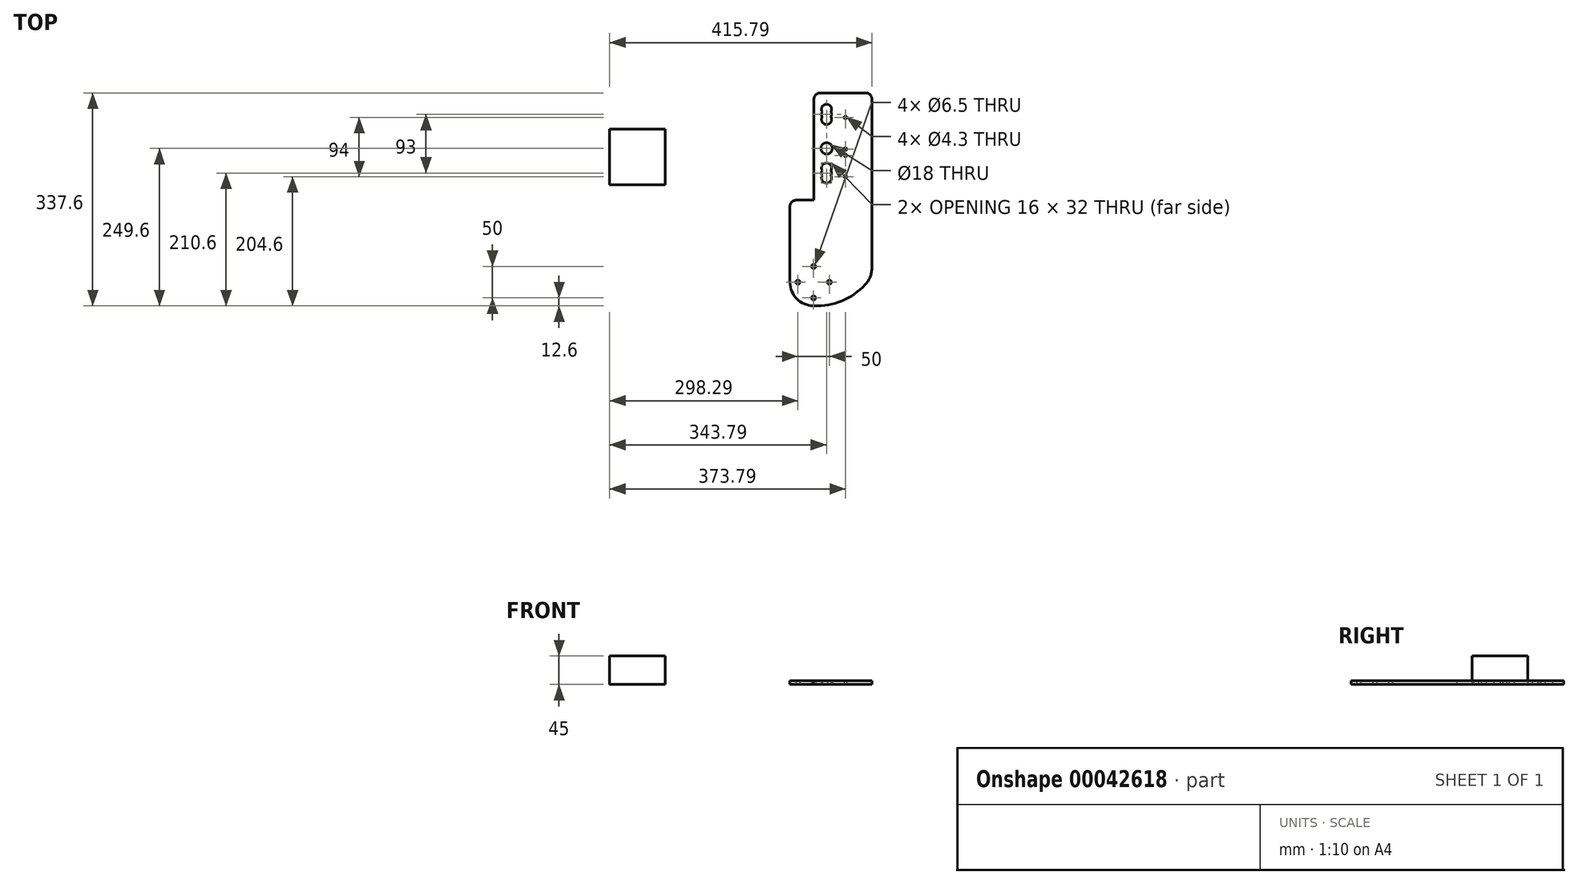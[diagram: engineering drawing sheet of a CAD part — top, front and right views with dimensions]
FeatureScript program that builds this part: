
annotation { "Feature Type Name" : "Feature", "Feature Type Description" : "" }
export const myFeature = defineFeature(function(context is Context, id is Id, definition is map)
    precondition{}
    {
        {
            var Q0;
            Q0=qCreatedBy(makeId("Top.planeOp"),FACE);
            var sketch = newSketch(context, id + "F0", { "sketchPlane" : qUnion([Q0])});
            skCircle(sketch, "E0", {"center": v(0, 0) * mm, "radius": 25 * mm, "construction": true});
            skLineSegment(sketch, "E1", {"start": v(-37.5, 0) * mm, "end": v(-37.5, 250) * mm});
            skLineSegment(sketch, "E2", {"start": v(-37.5, 0) * mm, "end": v(162.5, 0) * mm, "construction": true});
            skLineSegment(sketch, "E3.top", {"start": v(-27.5, 130) * mm, "end": v(50.5, 130) * mm});
            skLineSegment(sketch, "E3.left", {"start": v(-37.5, 29.98) * mm, "end": v(-37.5, 130) * mm});
            skLineSegment(sketch, "E3.right", {"start": v(50.5, 42) * mm, "end": v(50.5, 130) * mm, "construction": true});
            skLineSegment(sketch, "E4.bottom", {"start": v(-115.86, -29.09) * mm, "end": v(-157.06, -29.09) * mm});
            skLineSegment(sketch, "E4.top", {"start": v(-115.86, 126.35) * mm, "end": v(-157.06, 126.35) * mm});
            skLineSegment(sketch, "E4.left", {"start": v(-115.86, -29.09) * mm, "end": v(-115.86, 126.35) * mm});
            skLineSegment(sketch, "E4.right", {"start": v(-157.06, -29.09) * mm, "end": v(-157.06, 126.35) * mm});
            skPoint(sketch, "E5", {"position": v(-152.04, 2.91) * mm});
            skPoint(sketch, "E6", {"position": v(-152.03, 36.91) * mm});
            skPoint(sketch, "E7", {"position": v(-152.04, 46.91) * mm});
            skPoint(sketch, "E8", {"position": v(-152.05, 96.91) * mm});
            skLineSegment(sketch, "E9", {"start": v(50.5, 130) * mm, "end": v(50.5, 167) * mm, "construction": true});
            skLineSegment(sketch, "E10", {"start": v(50.5, 167) * mm, "end": v(50.5, 305.99) * mm, "construction": true});
            skPoint(sketch, "E11", {"position": v(50.5, 167) * mm});
            skPoint(sketch, "E12", {"position": v(50.5, 201) * mm});
            skPoint(sketch, "E13", {"position": v(50.5, 211) * mm});
            skPoint(sketch, "E14", {"position": v(50.5, 261) * mm});
            skLineSegment(sketch, "E15.bottom", {"start": v(50.5, 130) * mm, "end": v(92.5, 130) * mm, "construction": true});
            skLineSegment(sketch, "E15.top", {"start": v(50.5, 276) * mm, "end": v(92.5, 276) * mm, "construction": true});
            skLineSegment(sketch, "E15.left", {"start": v(50.5, 130) * mm, "end": v(50.5, 276) * mm, "construction": true});
            skLineSegment(sketch, "E15.right", {"start": v(92.5, 130) * mm, "end": v(92.5, 276) * mm, "construction": true});
            skLineSegment(sketch, "E16.0", {"start": v(20.5, 160) * mm, "end": v(20.5, 305.99) * mm, "construction": true});
            skPoint(sketch, "E17", {"position": v(20.5, 212) * mm});
            skPoint(sketch, "E18", {"position": v(20.5, 181) * mm});
            skPoint(sketch, "E19", {"position": v(20.5, 173) * mm});
            skPoint(sketch, "E20", {"position": v(20.5, 165) * mm});
            skPoint(sketch, "E21", {"position": v(20.5, 274) * mm});
            skPoint(sketch, "E22", {"position": v(20.5, 266) * mm});
            skPoint(sketch, "E23", {"position": v(20.5, 258) * mm});
            skCircle(sketch, "E24", {"center": v(50.5, 167) * mm, "radius": 2.15 * mm});
            skCircle(sketch, "E25", {"center": v(50.5, 201) * mm, "radius": 2.15 * mm});
            skCircle(sketch, "E26", {"center": v(50.5, 211) * mm, "radius": 2.15 * mm});
            skCircle(sketch, "E27", {"center": v(50.5, 261) * mm, "radius": 2.15 * mm});
            skCircle(sketch, "E28", {"center": v(20.5, 165) * mm, "radius": 8 * mm});
            skCircle(sketch, "E29", {"center": v(20.5, 173) * mm, "radius": 8 * mm});
            skCircle(sketch, "E30", {"center": v(20.5, 181) * mm, "radius": 8 * mm});
            skCircle(sketch, "E31", {"center": v(20.5, 212) * mm, "radius": 9 * mm});
            skCircle(sketch, "E32", {"center": v(20.5, 258) * mm, "radius": 8 * mm});
            skCircle(sketch, "E33", {"center": v(20.5, 266) * mm, "radius": 8 * mm});
            skCircle(sketch, "E34", {"center": v(20.5, 274) * mm, "radius": 8 * mm});
            skLineSegment(sketch, "E35.0", {"start": v(0.5, 160) * mm, "end": v(0.5, 290) * mm});
            skLineSegment(sketch, "E36", {"start": v(0.5, 143.81) * mm, "end": v(0.5, 160) * mm});
            skLineSegment(sketch, "E37", {"start": v(50.5, 276) * mm, "end": v(92.5, 276) * mm});
            skLineSegment(sketch, "E38", {"start": v(92.5, 130) * mm, "end": v(92.5, 290) * mm});
            skLineSegment(sketch, "E39", {"start": v(92.5, 130) * mm, "end": v(92.5, 75.52) * mm});
            skCircle(sketch, "E40", {"center": v(0, 0) * mm, "radius": 37.5 * mm, "construction": true});
            skCircle(sketch, "E41", {"center": v(25, 0) * mm, "radius": 3.25 * mm});
            skCircle(sketch, "E42.1.0", {"center": v(0, 25) * mm, "radius": 3.25 * mm});
            skCircle(sketch, "E42.2.0", {"center": v(-25, 0) * mm, "radius": 3.25 * mm});
            skCircle(sketch, "E42.3.0", {"center": v(0, -25) * mm, "radius": 3.25 * mm});
            skLineSegment(sketch, "E43", {"start": v(-37.5, 0) * mm, "end": v(-37.5, 120) * mm});
            skLineSegment(sketch, "E44", {"start": v(0.5, 130) * mm, "end": v(0.5, 293.83) * mm});
            skLineSegment(sketch, "E45", {"start": v(10.5, 300) * mm, "end": v(82.5, 300) * mm});
            skLineSegment(sketch, "E46", {"start": v(92.5, 286.82) * mm, "end": v(92.5, 23.32) * mm});
            skArc(sketch, "E47", {"start": v(0, -37.5) * mm, "mid": v(44.65, -29.7) * mm, "end": v(81.88, -3.83) * mm});
            skArc(sketch, "E48", {"start": v(-37.5, 0) * mm, "mid": v(-26.52, -26.52) * mm, "end": v(0, -37.5) * mm});
            skLineSegment(sketch, "E49", {"start": v(-37.5, 0) * mm, "end": v(-37.5, 130) * mm});
            skPoint(sketch, "E50.visualSharp", {"position": v(-37.5, 130) * mm});
            skArc(sketch, "E50.filletArc", {"start": v(-27.5, 130) * mm, "mid": v(-34.57, 127.07) * mm, "end": v(-37.5, 120) * mm});
            skArc(sketch, "E51.filletArc", {"start": v(10.5, 300) * mm, "mid": v(3.43, 297.07) * mm, "end": v(0.5, 290) * mm});
            skPoint(sketch, "E52.newPointA", {"position": v(92.5, 300) * mm});
            skArc(sketch, "E52.filletArc", {"start": v(92.5, 290) * mm, "mid": v(89.57, 297.07) * mm, "end": v(82.5, 300) * mm});
            skPoint(sketch, "E53.visualSharp", {"position": v(92.5, 9.75) * mm});
            skArc(sketch, "E53.filletArc", {"start": v(81.88, -3.83) * mm, "mid": v(89.75, 8.74) * mm, "end": v(92.5, 23.32) * mm});
            skLineSegment(sketch, "E54.bottom", {"start": v(-323.3, 242.43) * mm, "end": v(-235.3, 242.43) * mm});
            skLineSegment(sketch, "E54.top", {"start": v(-323.3, 154.43) * mm, "end": v(-235.3, 154.43) * mm});
            skLineSegment(sketch, "E54.left", {"start": v(-323.3, 242.43) * mm, "end": v(-323.3, 154.43) * mm});
            skLineSegment(sketch, "E54.right", {"start": v(-235.3, 242.43) * mm, "end": v(-235.3, 154.43) * mm});
            skSolve(sketch);
        }
        {
            var Q0;
            {var subQ0=sQuery(id+"F0.wireOp",EDGE,"D7nn4gsv-MtSc-hkAK-mBpY-22SBFaB82Joa");Q0=makeQuery(id+"F0.imprint","IMPRINT",FACE,{"disambiguationData":[TD([[makeQuery(id+"F0.imprint","IMPRINT",EDGE,{"derivedFrom":subQ0}),1.0]])]});}
            var Q1;
            Q1=makeQuery(id+"F0.imprint","IMPRINT",FACE,{"disambiguationData":[TD([[makeQuery(id+"F0.imprint","IMPRINT",EDGE,{"derivedFrom":sQuery(id+"F0.wireOp",EDGE,"E24")}),-1.0]])]});
            extrude(context, id + "F1", {"entities" : qUnion([Q0, Q1]), "depth" : 6 * mm});
        }
        {
            var Q0;
            Q0=makeQuery(id+"F0.imprint","IMPRINT",FACE,{"disambiguationData":[TD([[makeQuery(id+"F0.imprint","IMPRINT",EDGE,{"derivedFrom":sQuery(id+"F0.wireOp",EDGE,"E54.bottom")}),-1.0]])]});
            extrude(context, id + "F2", {"entities" : qUnion([Q0]), "depth" : 45 * mm});
        }
    });
